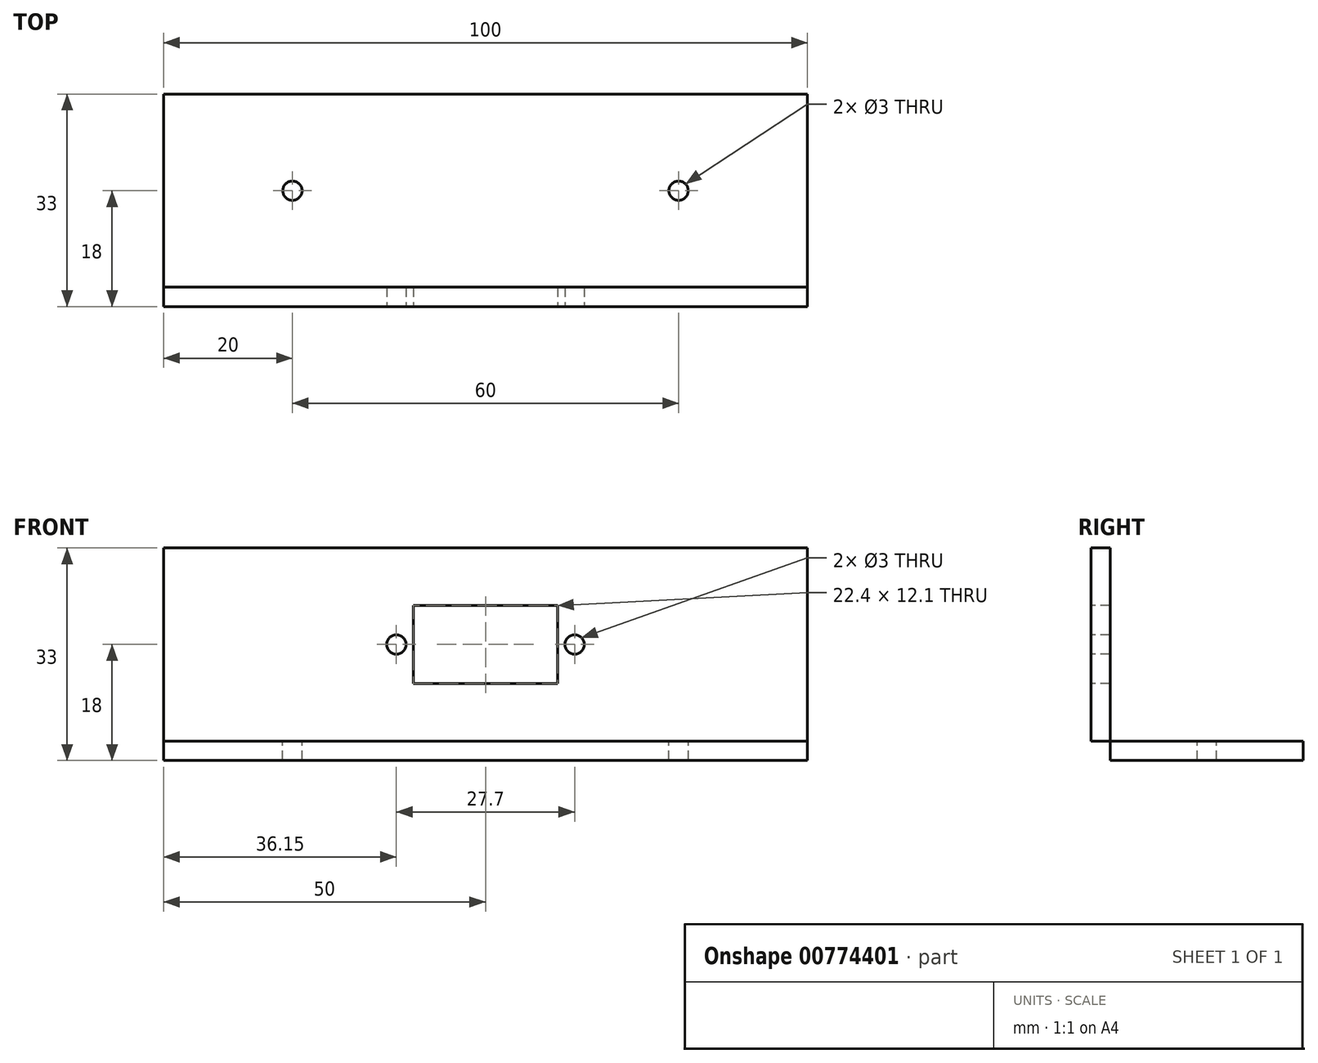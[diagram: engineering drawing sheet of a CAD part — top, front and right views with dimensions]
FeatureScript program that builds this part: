
annotation { "Feature Type Name" : "Feature", "Feature Type Description" : "" }
export const myFeature = defineFeature(function(context is Context, id is Id, definition is map)
    precondition{}
    {
        {
            var Q0;
            Q0=qCreatedBy(makeId("Top.planeOp"),FACE);
            var sketch = newSketch(context, id + "F0", { "sketchPlane" : qUnion([Q0])});
            skLineSegment(sketch, "E0.bottom", {"start": v(-50, 15) * mm, "end": v(50, 15) * mm});
            skLineSegment(sketch, "E0.top", {"start": v(-50, -15) * mm, "end": v(50, -15) * mm});
            skLineSegment(sketch, "E0.left", {"start": v(-50, 15) * mm, "end": v(-50, -15) * mm});
            skLineSegment(sketch, "E0.right", {"start": v(50, 15) * mm, "end": v(50, -15) * mm});
            skPoint(sketch, "E1", {"position": v(0, 0) * mm});
            skPoint(sketch, "E1.positionSnap0", {"position": v(-50, 0) * mm});
            skPoint(sketch, "E1.positionSnap1", {"position": v(0, 15) * mm});
            skSolve(sketch);
        }
        {
            var Q0;
            Q0 = qSketchRegion(id + "F0", true);
            extrude(context, id + "F1", {"entities" : qUnion([Q0]), "depth" : 3 * mm, "offsetDistance" : 25 * mm, "symmetric" : true});
        }
        {
            var Q0;
            Q0=makeQuery(id+"F1.opExtrude","SWEPT_FACE",FACE,{"disambiguationData":[OSD([sQuery(id+"F0.wireOp",EDGE,"E0.top")])]});
            var sketch = newSketch(context, id + "F2", { "sketchPlane" : qUnion([Q0])});
            skLineSegment(sketch, "E2.bottom", {"start": v(-50, 1.5) * mm, "end": v(50, 1.5) * mm});
            skLineSegment(sketch, "E2.top", {"start": v(-50, 31.5) * mm, "end": v(50, 31.5) * mm});
            skLineSegment(sketch, "E2.left", {"start": v(-50, 1.5) * mm, "end": v(-50, 31.5) * mm});
            skLineSegment(sketch, "E2.right", {"start": v(50, 1.5) * mm, "end": v(50, 31.5) * mm});
            skSolve(sketch);
        }
        {
            var Q0;
            Q0 = qSketchRegion(id + "F2", true);
            extrude(context, id + "F3", {"entities" : qUnion([Q0]), "depth" : 3 * mm, "offsetDistance" : 25 * mm});
        }
        {
            var Q0;
            Q0=makeQuery(id+"F3.opExtrude","CAP_FACE",FACE,{"disambiguationData":[OSD([sQuery(id+"F2.wireOp",EDGE,"E2.bottom"),sQuery(id+"F2.wireOp",EDGE,"E2.top"),sQuery(id+"F2.wireOp",EDGE,"E2.left"),sQuery(id+"F2.wireOp",EDGE,"E2.right")])],"isStart":false});
            var sketch = newSketch(context, id + "F4", { "sketchPlane" : qUnion([Q0])});
            skCircle(sketch, "E3", {"center": v(-13.85, 16.5) * mm, "radius": 1.5 * mm});
            skCircle(sketch, "E4", {"center": v(13.85, 16.5) * mm, "radius": 1.5 * mm});
            skLineSegment(sketch, "E5.bottom", {"start": v(-11.2, 22.55) * mm, "end": v(11.2, 22.55) * mm});
            skLineSegment(sketch, "E5.top", {"start": v(-11.2, 10.45) * mm, "end": v(11.2, 10.45) * mm});
            skLineSegment(sketch, "E5.left", {"start": v(-11.2, 22.55) * mm, "end": v(-11.2, 10.45) * mm});
            skLineSegment(sketch, "E5.right", {"start": v(11.2, 22.55) * mm, "end": v(11.2, 10.45) * mm});
            skPoint(sketch, "E6.positionSnap0", {"position": v(-11.2, 16.5) * mm});
            skPoint(sketch, "E7.positionSnap0", {"position": v(0, 31.5) * mm});
            skPoint(sketch, "E8", {"position": v(0, 22.55) * mm});
            skPoint(sketch, "E9", {"position": v(0, 10.45) * mm});
            skLineSegment(sketch, "E10", {"start": v(0, 22.55) * mm, "end": v(0, 10.45) * mm, "construction": true});
            skPoint(sketch, "E11", {"position": v(0, 16.5) * mm});
            skLineSegment(sketch, "E12", {"start": v(0, 31.5) * mm, "end": v(0, 1.5) * mm, "construction": true});
            skSolve(sketch);
        }
        {
            var Q0;
            Q0 = qSketchRegion(id + "F4", true);
            extrude(context, id + "F5", {"entities" : qUnion([Q0]), "operationType" : NewBodyOperationType.REMOVE, "endBound" : BoundingType.THROUGH_ALL, "oppositeDirection" : true, "depth" : 25 * mm, "offsetDistance" : 25 * mm});
        }
        {
            var Q0;
            Q0=makeQuery(id+"F1.opExtrude","CAP_FACE",FACE,{"disambiguationData":[OSD([sQuery(id+"F0.wireOp",EDGE,"E0.bottom"),sQuery(id+"F0.wireOp",EDGE,"E0.top"),sQuery(id+"F0.wireOp",EDGE,"E0.left"),sQuery(id+"F0.wireOp",EDGE,"E0.right")])],"isStart":false});
            var sketch = newSketch(context, id + "F6", { "sketchPlane" : qUnion([Q0])});
            skCircle(sketch, "E13", {"center": v(30, 0) * mm, "radius": 1.5 * mm});
            skPoint(sketch, "E13.centerSnap0", {"position": v(50, 0) * mm});
            skCircle(sketch, "E14", {"center": v(-30, 0) * mm, "radius": 1.5 * mm});
            skPoint(sketch, "E14.centerSnap0", {"position": v(-50, 0) * mm});
            skPoint(sketch, "E15", {"position": v(-33.38, 3.54) * mm});
            skPoint(sketch, "E16", {"position": v(-32.14, 3.87) * mm});
            skSolve(sketch);
        }
        {
            var Q0;
            Q0 = qSketchRegion(id + "F6", true);
            extrude(context, id + "F7", {"entities" : qUnion([Q0]), "operationType" : NewBodyOperationType.REMOVE, "endBound" : BoundingType.THROUGH_ALL, "oppositeDirection" : true, "depth" : 25 * mm, "offsetDistance" : 25 * mm});
        }
    });
